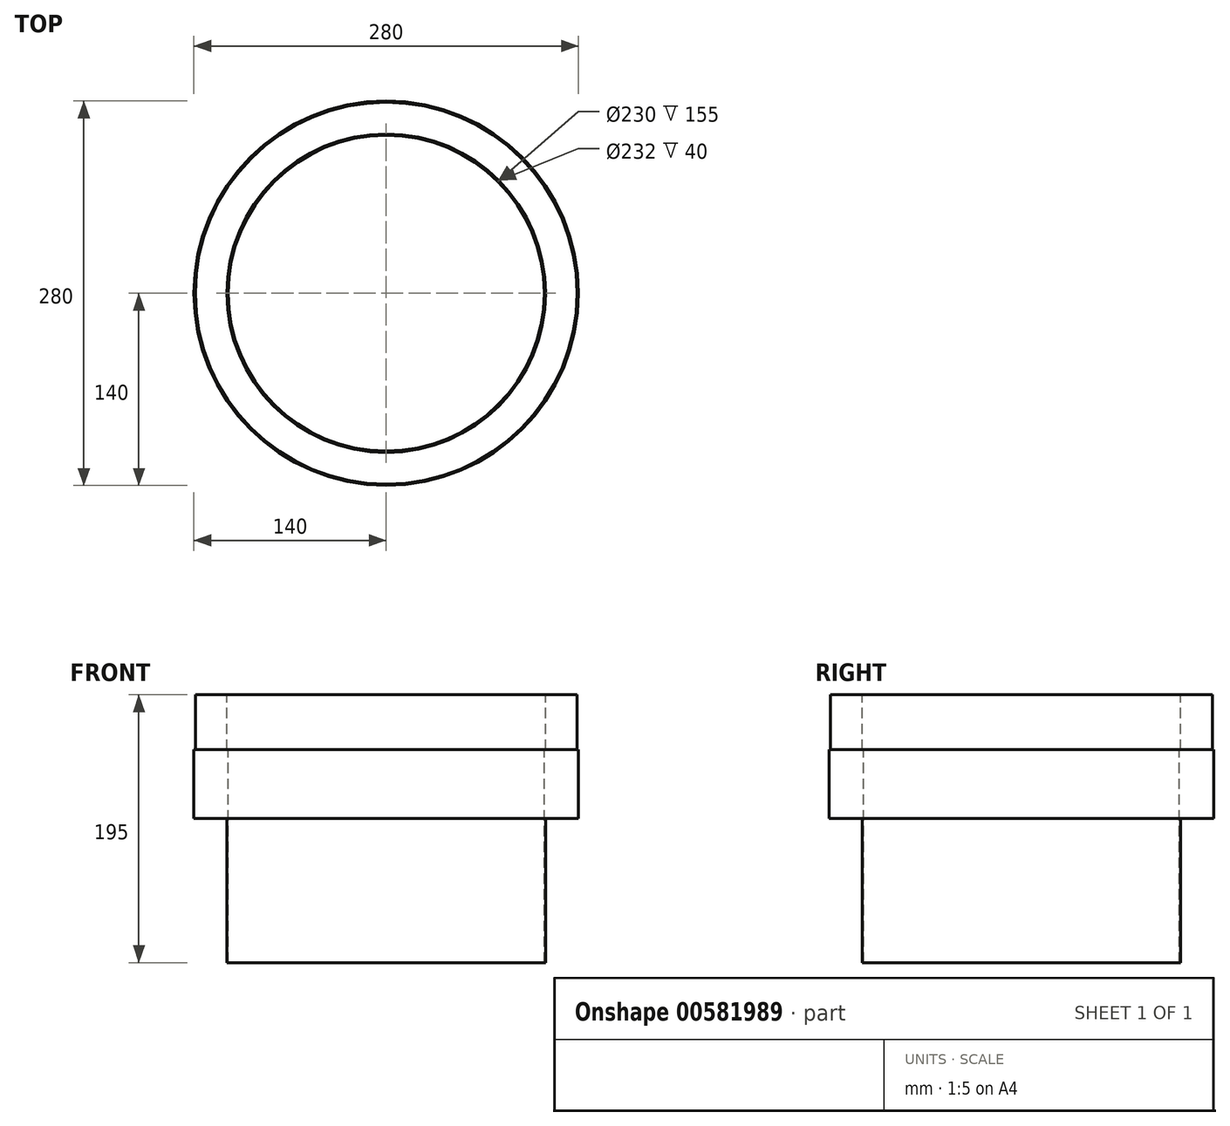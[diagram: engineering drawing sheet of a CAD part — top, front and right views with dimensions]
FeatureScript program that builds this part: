
annotation { "Feature Type Name" : "Feature", "Feature Type Description" : "" }
export const myFeature = defineFeature(function(context is Context, id is Id, definition is map)
    precondition{}
    {
        {
            var Q0;
            Q0=qCreatedBy(makeId("Front.planeOp"),FACE);
            var sketch = newSketch(context, id + "F0", { "sketchPlane" : qUnion([Q0])});
            skLineSegment(sketch, "E0", {"start": v(0, 710.75) * mm, "end": v(0, -704.58) * mm, "construction": true});
            skLineSegment(sketch, "E1", {"start": v(-115, 295.65) * mm, "end": v(-115, 410.65) * mm});
            skLineSegment(sketch, "E2", {"start": v(-115, 410.65) * mm, "end": v(-116, 410.65) * mm});
            skLineSegment(sketch, "E3", {"start": v(-139, 410.65) * mm, "end": v(-140, 410.65) * mm});
            skLineSegment(sketch, "E4", {"start": v(-140, 410.65) * mm, "end": v(-140, 360.65) * mm});
            skLineSegment(sketch, "E5", {"start": v(-140, 360.65) * mm, "end": v(-116, 360.65) * mm});
            skLineSegment(sketch, "E6", {"start": v(-116, 360.65) * mm, "end": v(-116, 295.65) * mm});
            skLineSegment(sketch, "E7", {"start": v(-139, 450.65) * mm, "end": v(-139, 410.65) * mm});
            skLineSegment(sketch, "E8", {"start": v(-139, 450.65) * mm, "end": v(-116, 450.65) * mm});
            skLineSegment(sketch, "E9", {"start": v(-116, 410.65) * mm, "end": v(-116, 450.65) * mm});
            skLineSegment(sketch, "E10", {"start": v(-115, 295.65) * mm, "end": v(-115, 255.65) * mm});
            skLineSegment(sketch, "E11", {"start": v(-116, 295.65) * mm, "end": v(-116, 255.65) * mm});
            skLineSegment(sketch, "E12", {"start": v(-116, 255.65) * mm, "end": v(-115, 255.65) * mm});
            skSolve(sketch);
        }
        {
            var Q0;
            Q0=qSketchRegion(id+"F0",true);
            var Q1;
            Q1=sQuery(id+"F0.wireOp",EDGE,"E0");
            revolve(context, id + "F1", {"entities" : qUnion([Q0]), "axis" : qUnion([Q1]), "revolveType" : RevolveType.FULL});
        }
    });
